FCSTD DOCUMENT  (FreeCAD 0.16R)
Label: Mk1
License: All rights reserved
LicenseURL: http://en.wikipedia.org/wiki/All_rights_reserved
objects: Sketcher::SketchObject×1
note: 1 computed .brp shape members not serialized (recipe doc carries the construction recipe); baked Part::Feature solids carry a one-line shape summary decoded from their .brp

FEATURE [Sketcher::SketchObject] Sketch
  sketch-geometry (23):
    g0: LineSegment StartX=-25 StartY=18 StartZ=0 EndX=25 EndY=18 EndZ=0
    g1: LineSegment StartX=25 StartY=18 StartZ=0 EndX=25 EndY=-18 EndZ=0
    g2: LineSegment StartX=25 StartY=-18 StartZ=0 EndX=-25 EndY=-18 EndZ=0
    g3: LineSegment StartX=-25 StartY=-18 StartZ=0 EndX=-25 EndY=18 EndZ=0
    g4: LineSegment StartX=25 StartY=-9 StartZ=0 EndX=60 EndY=-9 EndZ=0
    g5: LineSegment StartX=-25 StartY=9 StartZ=0 EndX=-60 EndY=9 EndZ=0
    g6: LineSegment StartX=-25 StartY=-9 StartZ=0 EndX=-60 EndY=-9 EndZ=0
    g7: LineSegment StartX=-60 StartY=24 StartZ=0 EndX=60 EndY=24 EndZ=0
    g8: LineSegment StartX=60 StartY=24 StartZ=0 EndX=60 EndY=-48 EndZ=0
    g9: LineSegment StartX=-60 StartY=24 StartZ=0 EndX=-60 EndY=-48 EndZ=0
    g10: LineSegment StartX=25 StartY=-18 StartZ=0 EndX=25 EndY=-48 EndZ=0
    g11: LineSegment StartX=-25 StartY=-18 StartZ=0 EndX=-25 EndY=-48 EndZ=0
    g12: LineSegment StartX=60 StartY=-48 StartZ=0 EndX=60 EndY=-48 EndZ=0
    g13: LineSegment StartX=-60 StartY=-27.7147 StartZ=0 EndX=-25 EndY=-27.7147 EndZ=0
    g14: LineSegment StartX=-60 StartY=-48 StartZ=0 EndX=60 EndY=-48 EndZ=0
    g15: LineSegment StartX=25 StartY=9 StartZ=0 EndX=60 EndY=9 EndZ=0
    g16: LineSegment StartX=-25 StartY=-26.6517 StartZ=0 EndX=25 EndY=-26.6517 EndZ=0
    g17: LineSegment StartX=-25 StartY=-37.1151 StartZ=0 EndX=25 EndY=-37.1151 EndZ=0
    g18: LineSegment StartX=0 StartY=-18 StartZ=0 EndX=0 EndY=-48 EndZ=0
    g19: LineSegment [constr] StartX=-39.5839 StartY=24 StartZ=0 EndX=-14.5839 EndY=24 EndZ=0
    g20: LineSegment [constr] StartX=-14.5839 StartY=24 StartZ=0 EndX=-14.5839 EndY=-51 EndZ=0
    g21: LineSegment [constr] StartX=-14.5839 StartY=-51 StartZ=0 EndX=-39.5839 EndY=-51 EndZ=0
    g22: LineSegment [constr] StartX=-39.5839 StartY=-51 StartZ=0 EndX=-39.5839 EndY=24 EndZ=0
  constraints (71):
    c: Coincident(g0,g1)
    c: Coincident(g1,g2)
    c: Coincident(g2,g3)
    c: Coincident(g3,g0)
    c: Horizontal(g0)
    c: Horizontal(g2)
    c: Vertical(g1)
    c: Vertical(g3)
    c: DistanceX(g0,g0) = 50
    c: Distance(g1) = 36
    c: Horizontal(g4)
    c: Horizontal(g5)
    c: Horizontal(g7)
    c: Coincident(g8,g7)
    c: Vertical(g8)
    c: Coincident(g9,g7)
    c: Vertical(g9)
    c: Coincident(g10,g1)
    c: Vertical(g10)
    c: Distance(g10) = 30
    c: Symmetric(g0,g2,g-1)
    c: Vertical(g11)
    c: Horizontal(g12)
    c: Coincident(g11,g2)
    c: PointOnObject(g6,g9)
    c: PointOnObject(g5,g9)
    c: Symmetric(g7,g7,g-2)
    c: PointOnObject(g13,g9)
    c: PointOnObject(g13,g11)
    c: Horizontal(g13)
    c: Distance(g13) = 35
    c: Coincident(g12,g8)
    c: Horizontal(g14)
    c: Coincident(g14,g8)
    c: Coincident(g14,g9)
    c: PointOnObject(g11,g14)
    c: PointOnObject(g10,g14)
    c: PointOnObject(g4,g1)
    c: PointOnObject(g4,g8)
    c: Horizontal(g15)
    c: PointOnObject(g15,g8)
    c: PointOnObject(g15,g1)
    c: PointOnObject(g5,g3)
    c: Horizontal(g6)
    c: PointOnObject(g6,g3)
    c: Symmetric(g15,g4,g-1)
    c: Symmetric(g5,g6,g-1)
    c: Distance(g15,g4) = 18
    c: Distance(g5,g6) = 18
    c: PointOnObject(g16,g11)
    c: PointOnObject(g16,g10)
    c: Horizontal(g16)
    c: PointOnObject(g17,g11)
    c: Horizontal(g17)
    c: PointOnObject(g17,g10)
    c: PointOnObject(g18,g2)
    c: PointOnObject(g18,g14)
    c: PointOnObject(g18,g-2)
    c: PointOnObject(g18,g-2)
    c: Coincident(g19,g20)
    c: Coincident(g20,g21)
    c: Coincident(g21,g22)
    c: Coincident(g22,g19)
    c: Horizontal(g19)
    c: Horizontal(g21)
    c: Vertical(g20)
    c: Vertical(g22)
    c: Distance(g19) = 25
    c: PointOnObject(g19,g7)
    c: Distance(g7,g8) = 72
    c: Distance(g22) = 75
